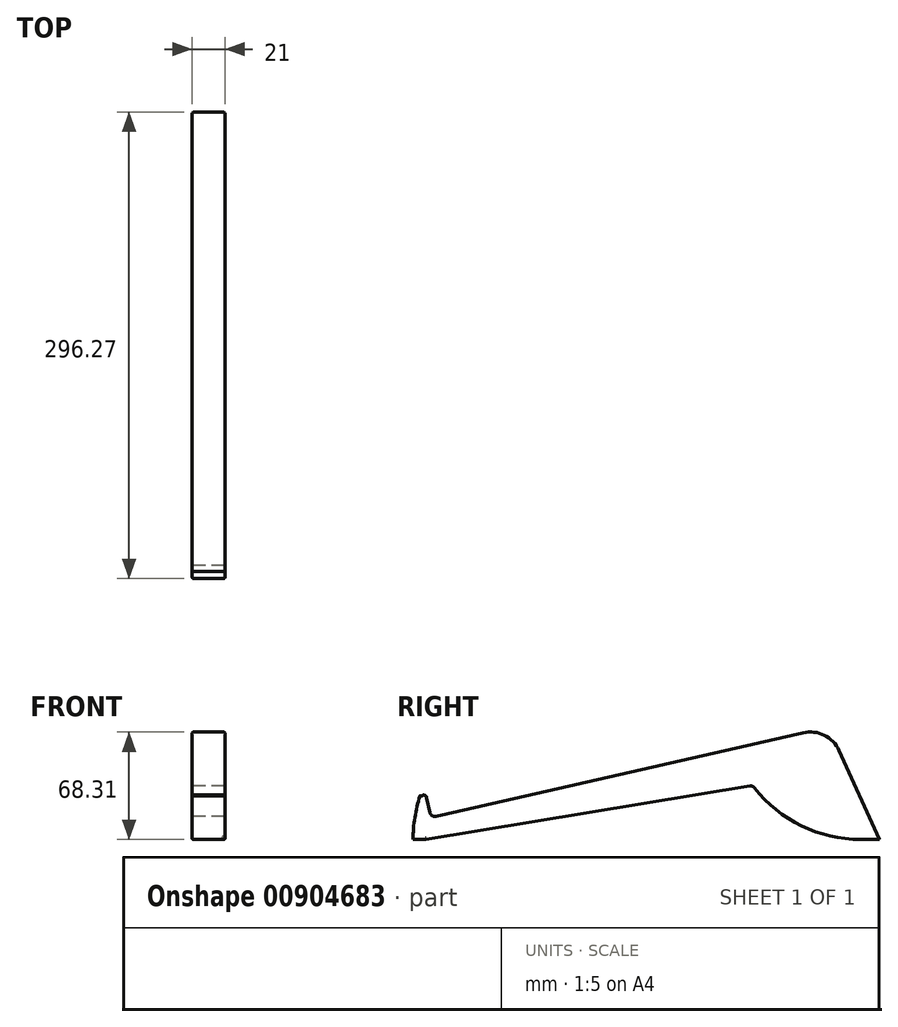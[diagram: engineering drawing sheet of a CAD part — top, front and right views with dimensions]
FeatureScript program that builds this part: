
annotation { "Feature Type Name" : "Feature", "Feature Type Description" : "" }
export const myFeature = defineFeature(function(context is Context, id is Id, definition is map)
    precondition{}
    {
        {
            var Q0;
            Q0=qCreatedBy(makeId("Right.planeOp"),FACE);
            var sketch = newSketch(context, id + "F0", { "sketchPlane" : qUnion([Q0])});
            skFitSpline(sketch, "E0", {"points": [v(155.17, -1.37) * mm, v(155.17, -1.37) * mm, v(155.17, -1.37) * mm, v(155.13, -1.27) * mm, v(129.5, 55.24) * mm, v(129.46, 55.33) * mm, v(129.46, 55.33) * mm, v(129.46, 55.33) * mm]});
            skLineSegment(sketch, "E1", {"start": v(-132.88, -1.37) * mm, "end": v(74.76, 32.91) * mm});
            skLineSegment(sketch, "E2", {"start": v(155.17, -1.37) * mm, "end": v(143.17, -1.37) * mm});
            skArc(sketch, "E3", {"start": v(74.76, 32.91) * mm, "mid": v(104.91, 7.68) * mm, "end": v(143.17, -1.37) * mm});
            skLineSegment(sketch, "E4", {"start": v(-132.88, -1.37) * mm, "end": v(-141.1, -1.37) * mm});
            skArc(sketch, "E5", {"start": v(-136.71, 26.37) * mm, "mid": v(-139.9, 12.66) * mm, "end": v(-141.1, -1.37) * mm});
            skLineSegment(sketch, "E6", {"start": v(-129.48, 12.63) * mm, "end": v(106.74, 66.44) * mm});
            skArc(sketch, "E7", {"start": v(129.56, 55.12) * mm, "mid": v(120.17, 64.84) * mm, "end": v(106.74, 66.44) * mm});
            skLineSegment(sketch, "E8", {"start": v(-136.71, 26.37) * mm, "end": v(-134.85, 26.79) * mm});
            skLineSegment(sketch, "E9", {"start": v(-129.48, 12.62) * mm, "end": v(-132.35, 25.22) * mm});
            skArc(sketch, "E10", {"start": v(-132.35, 25.22) * mm, "mid": v(-133.27, 26.52) * mm, "end": v(-134.85, 26.79) * mm});
            skSolve(sketch);
        }
        {
            var Q0;
            Q0=makeQuery(id+"F0.imprint","IMPRINT",FACE,{"disambiguationData":[TD([[makeQuery(id+"F0.imprint","IMPRINT",EDGE,{"derivedFrom":sQuery(id+"F0.wireOp",EDGE,"E0")}),1.0]])]});
            extrude(context, id + "F1", {"entities" : qUnion([Q0]), "depth" : 21 * mm, "offsetDistance" : 25 * mm});
        }
        {
            var Q0;
            Q0=makeQuery(id+"F1.opExtrude","SWEPT_EDGE",EDGE,{"disambiguationData":[OSD([sQuery(id+"F0.wireOp",EDGE,"E6"),sQuery(id+"F0.wireOp",EDGE,"E9")])]});
            var Q1;
            Q1=makeQuery(id+"F1.opExtrude","SWEPT_EDGE",EDGE,{"disambiguationData":[OSD([sQuery(id+"F0.wireOp",EDGE,"E1"),sQuery(id+"F0.wireOp",EDGE,"E3")])]});
            fillet(context, id + "F2", {"entities" : qUnion([Q0, Q1]), "radius" : 3 * mm, "tangentPropagation" : true, "allowEdgeOverflow" : false});
        }
        {
            var Q0;
            Q0=makeQuery(id+"F1.opExtrude","CAP_FACE",FACE,{"disambiguationData":[OSD([sQuery(id+"F0.wireOp",EDGE,"E0"),sQuery(id+"F0.wireOp",EDGE,"E1"),sQuery(id+"F0.wireOp",EDGE,"E2"),sQuery(id+"F0.wireOp",EDGE,"E3"),sQuery(id+"F0.wireOp",EDGE,"E4"),sQuery(id+"F0.wireOp",EDGE,"E5"),sQuery(id+"F0.wireOp",EDGE,"E6"),sQuery(id+"F0.wireOp",EDGE,"E7"),sQuery(id+"F0.wireOp",EDGE,"E8"),sQuery(id+"F0.wireOp",EDGE,"E9"),sQuery(id+"F0.wireOp",EDGE,"E10")])],"isStart":false});
            var Q1;
            Q1=makeQuery(id+"F1.opExtrude","CAP_FACE",FACE,{"disambiguationData":[OSD([sQuery(id+"F0.wireOp",EDGE,"E0"),sQuery(id+"F0.wireOp",EDGE,"E1"),sQuery(id+"F0.wireOp",EDGE,"E2"),sQuery(id+"F0.wireOp",EDGE,"E3"),sQuery(id+"F0.wireOp",EDGE,"E4"),sQuery(id+"F0.wireOp",EDGE,"E5"),sQuery(id+"F0.wireOp",EDGE,"E6"),sQuery(id+"F0.wireOp",EDGE,"E7"),sQuery(id+"F0.wireOp",EDGE,"E8"),sQuery(id+"F0.wireOp",EDGE,"E9"),sQuery(id+"F0.wireOp",EDGE,"E10")])],"isStart":true});
            fillet(context, id + "F3", {"entities" : qUnion([Q0, Q1]), "radius" : 1 * mm, "tangentPropagation" : true, "allowEdgeOverflow" : false});
        }
    });
